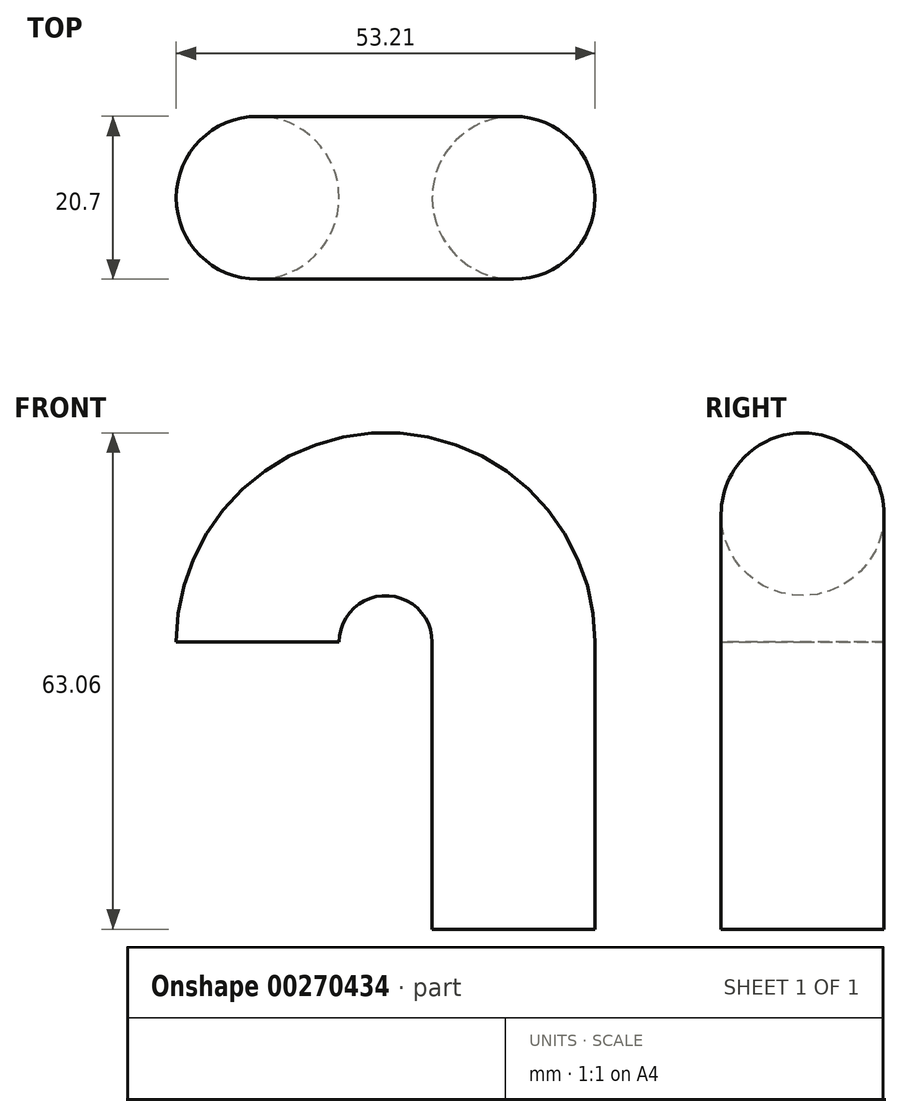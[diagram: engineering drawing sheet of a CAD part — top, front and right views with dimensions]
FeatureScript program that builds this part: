
annotation { "Feature Type Name" : "Feature", "Feature Type Description" : "" }
export const myFeature = defineFeature(function(context is Context, id is Id, definition is map)
    precondition{}
    {
        {
            var Q0;
            Q0=qCreatedBy(makeId("Front.planeOp"),FACE);
            var sketch = newSketch(context, id + "F0", { "sketchPlane" : qUnion([Q0])});
            skLineSegment(sketch, "E0", {"start": v(0, 0) * mm, "end": v(0, 36.46) * mm});
            skArc(sketch, "E1", {"start": v(0, 36.46) * mm, "mid": v(-16.26, 52.72) * mm, "end": v(-32.52, 36.46) * mm});
            skSolve(sketch);
        }
        {
            var Q0;
            Q0=qCreatedBy(makeId("Top.planeOp"),FACE);
            var sketch = newSketch(context, id + "F1", { "sketchPlane" : qUnion([Q0])});
            skCircle(sketch, "E2", {"center": v(0, 0) * mm, "radius": 10.35 * mm});
            skSolve(sketch);
        }
        {
            var Q0;
            Q0=makeQuery(id+"F1.imprint","IMPRINT",FACE,{"disambiguationData":[TD([[makeQuery(id+"F1.imprint","IMPRINT",EDGE,{"derivedFrom":sQuery(id+"F1.wireOp",EDGE,"E2")}),1.0]])]});
            var Q1;
            Q1=sQuery(id+"F0.wireOp",EDGE,"E0");
            var Q2;
            Q2=sQuery(id+"F0.wireOp",EDGE,"E1");
            sweep(context, id + "F2", {"profiles" : qUnion([Q0]), "path" : qUnion([Q1, Q2])});
        }
    });
